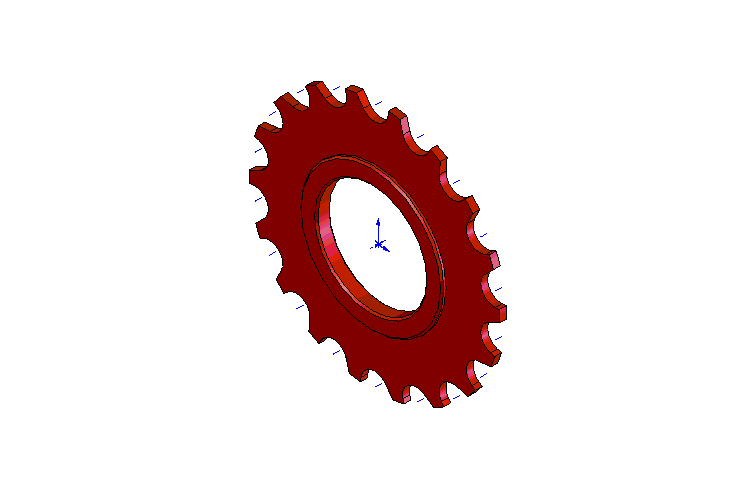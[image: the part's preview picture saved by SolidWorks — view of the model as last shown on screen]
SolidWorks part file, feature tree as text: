
SOLIDWORKS PART (.sldprt)
format: sldprt  version: not decoded by parser v0  size: 242,688 bytes
history: native  units: mm
features: sketch x4, plane x3, extrude x3, material x1, cut_extrude x1, pattern_circular x1, chamfer x1 (+10 scaffold rows collapsed)
feature tree (24):
  scaffold x10  (default folders/planes/origin — collapsed)
  material  "Matériau <non spécifié>"
  plane  "Plan de face"
  plane  "Plan de dessus"
  plane  "Plan de droite"
  sketch  "Esquisse1"  dims[D1=73.5mm]
  extrude  "Extrusion1"  Depth=2mm
  sketch  "Esquisse2"  dims[c1.D1=8.0mm c1.D3=4.0mm c2.D1=8.0mm c2.D3=4.0mm c2.D2=9.5mm c3.D3=4.0mm c3.D2=~2.039916mm c4.D2=35.0deg c4.D3=5.0mm]
  cut_extrude  "Enlèv. mat.-Extru.1"  [1 undecoded]
  pattern_circular  "Répétition circulaire1"  Count=18 Angle=20deg
  sketch  "Esquisse3"  dims[D1=42.0mm]
  extrude  "Extrusion2"  Depth=4.25mm
  sketch  "Esquisse4"  dims[D1=32.0mm]
  extrude  "Enlèv. mat.-Extru.2"  [1 undecoded]
  chamfer  "Chanfrein1"  Distance=0.5mm Angle=45deg
decode coverage: 8 of 10 modeling features carry decoded parameters
note: ~ marks probable driven/reference dimensions
note: 2 parameter values undecoded
note: suppression state not decoded; provenance and decode notes live in map.json
